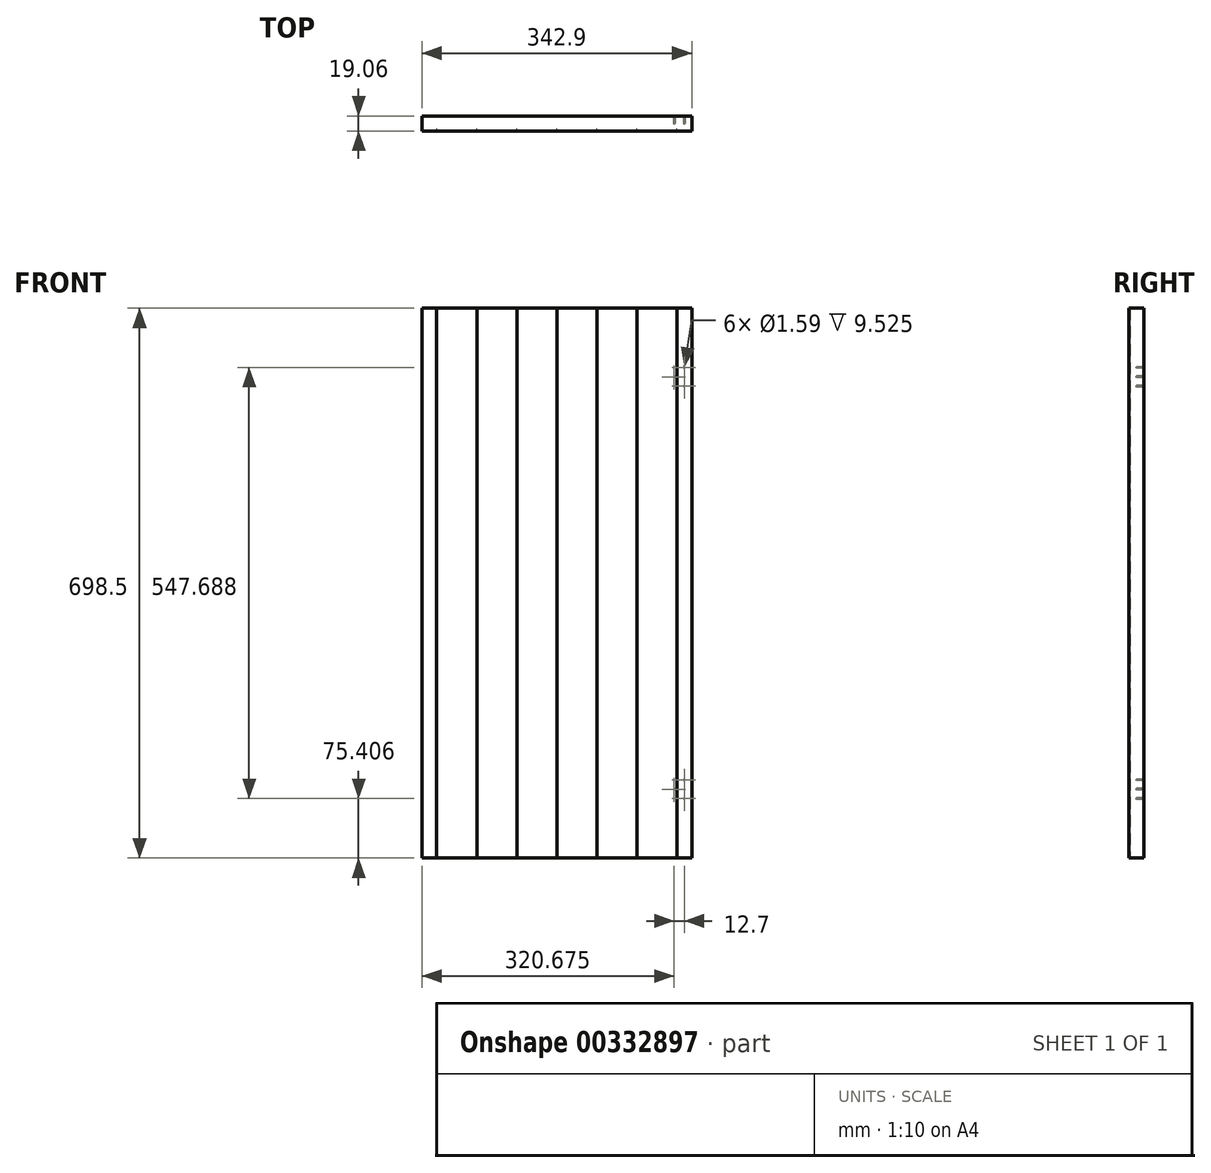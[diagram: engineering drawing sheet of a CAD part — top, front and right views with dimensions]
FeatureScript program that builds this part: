
annotation { "Feature Type Name" : "Feature", "Feature Type Description" : "" }
export const myFeature = defineFeature(function(context is Context, id is Id, definition is map)
    precondition{}
    {
        {
            var Q0;
            Q0=qCreatedBy(makeId("Top.planeOp"),FACE);
            var sketch = newSketch(context, id + "F0", { "sketchPlane" : qUnion([Q0])});
            skLineSegment(sketch, "E0.bottom", {"start": v(508, -9.53) * mm, "end": v(458.22, -9.53) * mm});
            skLineSegment(sketch, "E0.top", {"start": v(508, 9.53) * mm, "end": v(-508, 9.53) * mm});
            skLineSegment(sketch, "E0.left", {"start": v(508, 9.53) * mm, "end": v(508, -9.53) * mm});
            skLineSegment(sketch, "E0.right", {"start": v(-508, 9.53) * mm, "end": v(-508, -9.53) * mm});
            skPoint(sketch, "E0.middle", {"position": v(0, 0) * mm});
            skArc(sketch, "E1", {"start": v(-509.02, -9.53) * mm, "mid": v(-508.3, -9.23) * mm, "end": v(-508, -8.5) * mm});
            skArc(sketch, "E2", {"start": v(-508, -8.5) * mm, "mid": v(-507.7, -9.23) * mm, "end": v(-506.98, -9.52) * mm});
            skArc(sketch, "E3.1.0.0", {"start": v(-458.22, -9.53) * mm, "mid": v(-457.5, -9.23) * mm, "end": v(-457.2, -8.5) * mm});
            skArc(sketch, "E3.1.0.1", {"start": v(-457.2, -8.5) * mm, "mid": v(-456.9, -9.23) * mm, "end": v(-456.18, -9.52) * mm});
            skArc(sketch, "E3.2.0.0", {"start": v(-407.42, -9.53) * mm, "mid": v(-406.7, -9.23) * mm, "end": v(-406.4, -8.5) * mm});
            skArc(sketch, "E3.2.0.1", {"start": v(-406.4, -8.5) * mm, "mid": v(-406.1, -9.23) * mm, "end": v(-405.38, -9.52) * mm});
            skArc(sketch, "E3.3.0.0", {"start": v(-356.62, -9.53) * mm, "mid": v(-355.9, -9.23) * mm, "end": v(-355.6, -8.5) * mm});
            skArc(sketch, "E3.3.0.1", {"start": v(-355.6, -8.5) * mm, "mid": v(-355.3, -9.23) * mm, "end": v(-354.58, -9.52) * mm});
            skArc(sketch, "E3.4.0.0", {"start": v(-305.82, -9.53) * mm, "mid": v(-305.1, -9.23) * mm, "end": v(-304.8, -8.5) * mm});
            skArc(sketch, "E3.4.0.1", {"start": v(-304.8, -8.5) * mm, "mid": v(-304.5, -9.23) * mm, "end": v(-303.78, -9.52) * mm});
            skArc(sketch, "E3.5.0.0", {"start": v(-255.02, -9.53) * mm, "mid": v(-254.3, -9.23) * mm, "end": v(-254, -8.5) * mm});
            skArc(sketch, "E3.5.0.1", {"start": v(-254, -8.5) * mm, "mid": v(-253.7, -9.23) * mm, "end": v(-252.98, -9.52) * mm});
            skArc(sketch, "E3.6.0.0", {"start": v(-204.22, -9.53) * mm, "mid": v(-203.5, -9.23) * mm, "end": v(-203.2, -8.5) * mm});
            skArc(sketch, "E3.6.0.1", {"start": v(-203.2, -8.5) * mm, "mid": v(-202.9, -9.23) * mm, "end": v(-202.18, -9.52) * mm});
            skArc(sketch, "E3.7.0.0", {"start": v(-153.42, -9.53) * mm, "mid": v(-152.7, -9.23) * mm, "end": v(-152.4, -8.5) * mm});
            skArc(sketch, "E3.7.0.1", {"start": v(-152.4, -8.5) * mm, "mid": v(-152.1, -9.23) * mm, "end": v(-151.38, -9.52) * mm});
            skArc(sketch, "E3.8.0.0", {"start": v(-102.62, -9.53) * mm, "mid": v(-101.9, -9.23) * mm, "end": v(-101.6, -8.5) * mm});
            skArc(sketch, "E3.8.0.1", {"start": v(-101.6, -8.5) * mm, "mid": v(-101.3, -9.23) * mm, "end": v(-100.58, -9.52) * mm});
            skArc(sketch, "E3.9.0.0", {"start": v(-51.82, -9.53) * mm, "mid": v(-51.1, -9.23) * mm, "end": v(-50.8, -8.5) * mm});
            skArc(sketch, "E3.9.0.1", {"start": v(-50.8, -8.5) * mm, "mid": v(-50.5, -9.23) * mm, "end": v(-49.78, -9.52) * mm});
            skArc(sketch, "E3.10.0.0", {"start": v(-1.02, -9.53) * mm, "mid": v(-0.3, -9.23) * mm, "end": v(0, -8.5) * mm});
            skArc(sketch, "E3.10.0.1", {"start": v(0, -8.5) * mm, "mid": v(0.3, -9.23) * mm, "end": v(1.02, -9.52) * mm});
            skArc(sketch, "E3.11.0.0", {"start": v(49.78, -9.53) * mm, "mid": v(50.5, -9.23) * mm, "end": v(50.8, -8.5) * mm});
            skArc(sketch, "E3.11.0.1", {"start": v(50.8, -8.5) * mm, "mid": v(51.1, -9.23) * mm, "end": v(51.82, -9.52) * mm});
            skArc(sketch, "E3.12.0.0", {"start": v(100.58, -9.53) * mm, "mid": v(101.3, -9.23) * mm, "end": v(101.6, -8.5) * mm});
            skArc(sketch, "E3.12.0.1", {"start": v(101.6, -8.5) * mm, "mid": v(101.9, -9.23) * mm, "end": v(102.62, -9.52) * mm});
            skArc(sketch, "E3.13.0.0", {"start": v(151.38, -9.53) * mm, "mid": v(152.1, -9.23) * mm, "end": v(152.4, -8.5) * mm});
            skArc(sketch, "E3.13.0.1", {"start": v(152.4, -8.5) * mm, "mid": v(152.7, -9.23) * mm, "end": v(153.42, -9.52) * mm});
            skArc(sketch, "E3.14.0.0", {"start": v(202.18, -9.53) * mm, "mid": v(202.9, -9.23) * mm, "end": v(203.2, -8.5) * mm});
            skArc(sketch, "E3.14.0.1", {"start": v(203.2, -8.5) * mm, "mid": v(203.5, -9.23) * mm, "end": v(204.22, -9.52) * mm});
            skArc(sketch, "E3.15.0.0", {"start": v(252.98, -9.53) * mm, "mid": v(253.7, -9.23) * mm, "end": v(254, -8.5) * mm});
            skArc(sketch, "E3.15.0.1", {"start": v(254, -8.5) * mm, "mid": v(254.3, -9.23) * mm, "end": v(255.02, -9.52) * mm});
            skArc(sketch, "E3.16.0.0", {"start": v(303.78, -9.53) * mm, "mid": v(304.5, -9.23) * mm, "end": v(304.8, -8.5) * mm});
            skArc(sketch, "E3.16.0.1", {"start": v(304.8, -8.5) * mm, "mid": v(305.1, -9.23) * mm, "end": v(305.82, -9.52) * mm});
            skArc(sketch, "E3.17.0.0", {"start": v(354.58, -9.53) * mm, "mid": v(355.3, -9.23) * mm, "end": v(355.6, -8.5) * mm});
            skArc(sketch, "E3.17.0.1", {"start": v(355.6, -8.5) * mm, "mid": v(355.9, -9.23) * mm, "end": v(356.62, -9.52) * mm});
            skArc(sketch, "E3.18.0.0", {"start": v(405.38, -9.53) * mm, "mid": v(406.1, -9.23) * mm, "end": v(406.4, -8.5) * mm});
            skArc(sketch, "E3.18.0.1", {"start": v(406.4, -8.5) * mm, "mid": v(406.7, -9.23) * mm, "end": v(407.42, -9.52) * mm});
            skArc(sketch, "E3.19.0.0", {"start": v(456.18, -9.53) * mm, "mid": v(456.9, -9.23) * mm, "end": v(457.2, -8.5) * mm});
            skArc(sketch, "E3.19.0.1", {"start": v(457.2, -8.5) * mm, "mid": v(457.5, -9.23) * mm, "end": v(458.22, -9.52) * mm});
            skLineSegment(sketch, "E3.direction1", {"start": v(-506.98, -9.53) * mm, "end": v(-458.22, -9.53) * mm, "construction": true});
            skLineSegment(sketch, "E4.trimOffspring", {"start": v(-458.22, -9.53) * mm, "end": v(-508, -9.53) * mm});
            skLineSegment(sketch, "E5.trimOffspring", {"start": v(-407.42, -9.53) * mm, "end": v(-456.18, -9.53) * mm});
            skLineSegment(sketch, "E6.trimOffspring", {"start": v(-356.62, -9.53) * mm, "end": v(-405.38, -9.53) * mm});
            skLineSegment(sketch, "E7.trimOffspring", {"start": v(-305.82, -9.53) * mm, "end": v(-354.58, -9.53) * mm});
            skLineSegment(sketch, "E8.trimOffspring", {"start": v(-255.02, -9.53) * mm, "end": v(-303.78, -9.53) * mm});
            skLineSegment(sketch, "E9.trimOffspring", {"start": v(-204.22, -9.53) * mm, "end": v(-252.98, -9.53) * mm});
            skLineSegment(sketch, "E10.trimOffspring", {"start": v(-153.42, -9.53) * mm, "end": v(-202.18, -9.53) * mm});
            skLineSegment(sketch, "E11.trimOffspring", {"start": v(-102.62, -9.53) * mm, "end": v(-151.38, -9.53) * mm});
            skLineSegment(sketch, "E12.trimOffspring", {"start": v(-51.82, -9.53) * mm, "end": v(-100.58, -9.53) * mm});
            skLineSegment(sketch, "E13.trimOffspring", {"start": v(-1.02, -9.53) * mm, "end": v(-49.78, -9.53) * mm});
            skLineSegment(sketch, "E14.trimOffspring", {"start": v(49.78, -9.53) * mm, "end": v(1.02, -9.53) * mm});
            skLineSegment(sketch, "E15.trimOffspring", {"start": v(100.58, -9.53) * mm, "end": v(51.82, -9.53) * mm});
            skLineSegment(sketch, "E16.trimOffspring", {"start": v(151.38, -9.53) * mm, "end": v(102.62, -9.53) * mm});
            skLineSegment(sketch, "E17.trimOffspring", {"start": v(202.18, -9.53) * mm, "end": v(153.42, -9.53) * mm});
            skLineSegment(sketch, "E18.trimOffspring", {"start": v(252.98, -9.53) * mm, "end": v(204.22, -9.53) * mm});
            skLineSegment(sketch, "E19.trimOffspring", {"start": v(303.78, -9.53) * mm, "end": v(255.02, -9.53) * mm});
            skLineSegment(sketch, "E20.trimOffspring", {"start": v(354.58, -9.53) * mm, "end": v(305.82, -9.53) * mm});
            skLineSegment(sketch, "E21.trimOffspring", {"start": v(405.38, -9.53) * mm, "end": v(356.62, -9.53) * mm});
            skLineSegment(sketch, "E22.trimOffspring", {"start": v(456.18, -9.53) * mm, "end": v(407.42, -9.53) * mm});
            skSolve(sketch);
        }
        {
            var Q0;
            Q0=qSketchRegion(id+"F0",true);
            extrude(context, id + "F1", {"entities" : qUnion([Q0]), "depth" : 698.5 * mm});
        }
        {
            var Q0;
            Q0=qCreatedBy(makeId("Top.planeOp"),FACE);
            var sketch = newSketch(context, id + "F2", { "sketchPlane" : qUnion([Q0])});
            skLineSegment(sketch, "E23.bottom", {"start": v(171.45, -89.59) * mm, "end": v(679.45, -89.59) * mm});
            skLineSegment(sketch, "E23.top", {"start": v(171.45, 47.64) * mm, "end": v(679.45, 47.64) * mm});
            skLineSegment(sketch, "E23.left", {"start": v(171.45, -89.59) * mm, "end": v(171.45, 47.64) * mm});
            skLineSegment(sketch, "E23.right", {"start": v(679.45, -89.59) * mm, "end": v(679.45, 47.64) * mm});
            skLineSegment(sketch, "E24.bottom", {"start": v(-171.45, -137.09) * mm, "end": v(-679.45, -137.09) * mm});
            skLineSegment(sketch, "E24.top", {"start": v(-171.45, 58.2) * mm, "end": v(-679.45, 58.2) * mm});
            skLineSegment(sketch, "E24.left", {"start": v(-171.45, -137.09) * mm, "end": v(-171.45, 58.2) * mm});
            skLineSegment(sketch, "E24.right", {"start": v(-679.45, -137.09) * mm, "end": v(-679.45, 58.2) * mm});
            skSolve(sketch);
        }
        {
            var Q0;
            Q0=qSketchRegion(id+"F2",true);
            extrude(context, id + "F3", {"entities" : qUnion([Q0]), "operationType" : NewBodyOperationType.REMOVE, "depth" : 1143 * mm});
        }
        {
            var Q0;
            Q0=qCreatedBy(makeId("Front.planeOp"),FACE);
            var sketch = newSketch(context, id + "F4", { "sketchPlane" : qUnion([Q0])});
            skLineSegment(sketch, "E25.bottom", {"start": v(149.23, 0) * mm, "end": v(161.93, 0) * mm, "construction": true});
            skLineSegment(sketch, "E25.top", {"start": v(161.92, 698.5) * mm, "end": v(168.27, 698.5) * mm, "construction": true});
            skLineSegment(sketch, "E25.left", {"start": v(149.23, 0) * mm, "end": v(149.22, 623.1) * mm, "construction": true});
            skLineSegment(sketch, "E25.right", {"start": v(161.93, 0) * mm, "end": v(161.92, 698.5) * mm, "construction": true});
            skLineSegment(sketch, "E26", {"start": v(149.22, 611.19) * mm, "end": v(148.43, 611.19) * mm, "construction": true});
            skLineSegment(sketch, "E27", {"start": v(161.93, 623.1) * mm, "end": v(149.22, 623.1) * mm, "construction": true});
            skLineSegment(sketch, "E28", {"start": v(149.22, 599.28) * mm, "end": v(161.93, 599.28) * mm, "construction": true});
            skCircle(sketch, "E29", {"center": v(161.93, 623.1) * mm, "radius": 0.8 * mm});
            skCircle(sketch, "E30", {"center": v(149.22, 611.19) * mm, "radius": 0.8 * mm});
            skCircle(sketch, "E31", {"center": v(161.93, 599.28) * mm, "radius": 0.8 * mm});
            skCircle(sketch, "E32", {"center": v(161.93, 99.22) * mm, "radius": 0.8 * mm});
            skCircle(sketch, "E33", {"center": v(149.23, 87.31) * mm, "radius": 0.8 * mm});
            skCircle(sketch, "E34", {"center": v(161.93, 75.4) * mm, "radius": 0.8 * mm});
            skSolve(sketch);
        }
        {
            var Q0;
            Q0=qSketchRegion(id+"F4",true);
            extrude(context, id + "F5", {"entities" : qUnion([Q0]), "operationType" : NewBodyOperationType.REMOVE, "oppositeDirection" : true, "depth" : 25.4 * mm});
        }
    });
